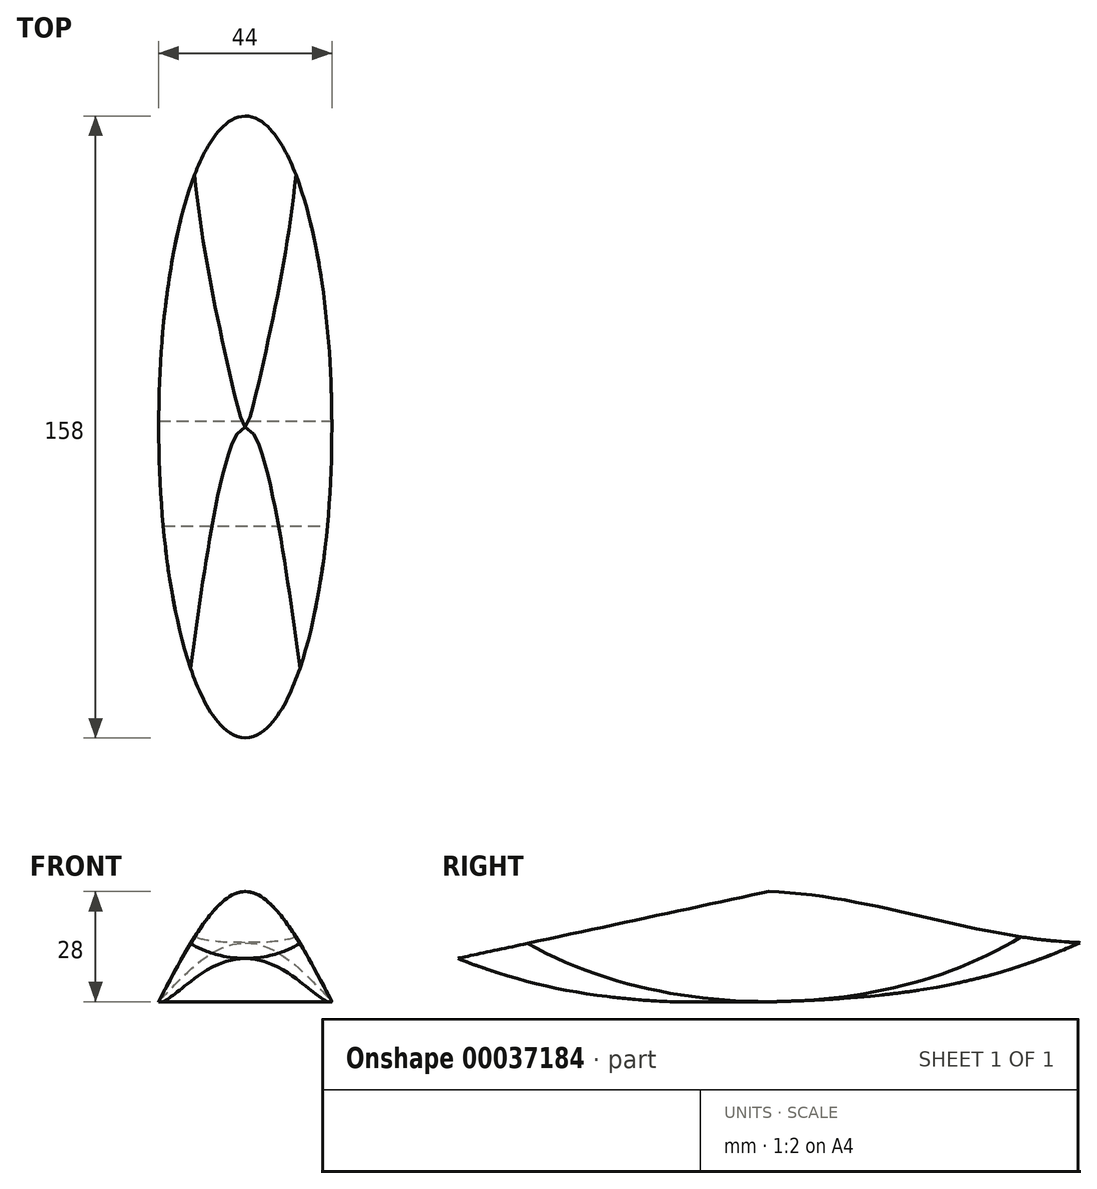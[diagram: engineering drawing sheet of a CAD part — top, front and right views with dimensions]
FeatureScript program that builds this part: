
annotation { "Feature Type Name" : "Feature", "Feature Type Description" : "" }
export const myFeature = defineFeature(function(context is Context, id is Id, definition is map)
    precondition{}
    {
        {
            var Q0;
            Q0=qCreatedBy(makeId("Top.planeOp"),FACE);
            var sketch = newSketch(context, id + "F0", { "sketchPlane" : qUnion([Q0])});
            skEllipse(sketch, "E0", {"center": v(0, 0) * mm, "majorRadius": 22 * mm, "minorRadius": 79 * mm, "majorAxis": v(-1, 0)});
            skSolve(sketch);
        }
        {
            var Q0;
            Q0=qCreatedBy(makeId("Right.planeOp"),FACE);
            var sketch = newSketch(context, id + "F1", { "sketchPlane" : qUnion([Q0])});
            skFitSpline(sketch, "E1", {"points": [v(79, 15) * mm, v(0, 28) * mm], "startDerivative": vector(-81.5, 3) * mm, "endDerivative": vector(-81.5, 3) * mm});
            skLineSegment(sketch, "E2", {"start": v(0, 28) * mm, "end": v(-79, 11) * mm});
            skFitSpline(sketch, "E3", {"points": [v(-79, 11) * mm, v(1.53, 0) * mm, v(79, 15) * mm], "startDerivative": vector(166.06, -67.38) * mm, "endDerivative": vector(159.92, 73.68) * mm});
            skSolve(sketch);
        }
        {
            var Q0;
            Q0=qCreatedBy(makeId("Front.planeOp"),FACE);
            var sketch = newSketch(context, id + "F2", { "sketchPlane" : qUnion([Q0])});
            skFitSpline(sketch, "E4", {"points": [v(-22, 0) * mm, v(0, 28) * mm, v(22, 0) * mm], "startDerivative": vector(44, 84) * mm, "endDerivative": vector(44, -84) * mm});
            skLineSegment(sketch, "E5", {"start": v(-22, 0) * mm, "end": v(22, 0) * mm});
            skSolve(sketch);
        }
        {
            var Q0;
            Q0 = qSketchRegion(id + "F0", true);
            extrude(context, id + "F3", {"entities" : qUnion([Q0]), "depth" : 28 * 2 * mm});
        }
        {
            var Q0;
            Q0 = qSketchRegion(id + "F1", true);
            extrude(context, id + "F4", {"entities" : qUnion([Q0]), "operationType" : NewBodyOperationType.INTERSECT, "oppositeDirection" : true, "depth" : 44 * 2 * mm, "symmetric" : true});
        }
        {
            var Q0;
            Q0 = qSketchRegion(id + "F2", true);
            extrude(context, id + "F5", {"entities" : qUnion([Q0]), "operationType" : NewBodyOperationType.INTERSECT, "oppositeDirection" : true, "depth" : 163 * 2 * mm, "hasSecondDirection" : true, "secondDirectionBound" : BoundingType.THROUGH_ALL, "secondDirectionOppositeDirection" : false, "secondDirectionDepth" : 25 * mm});
        }
    });
